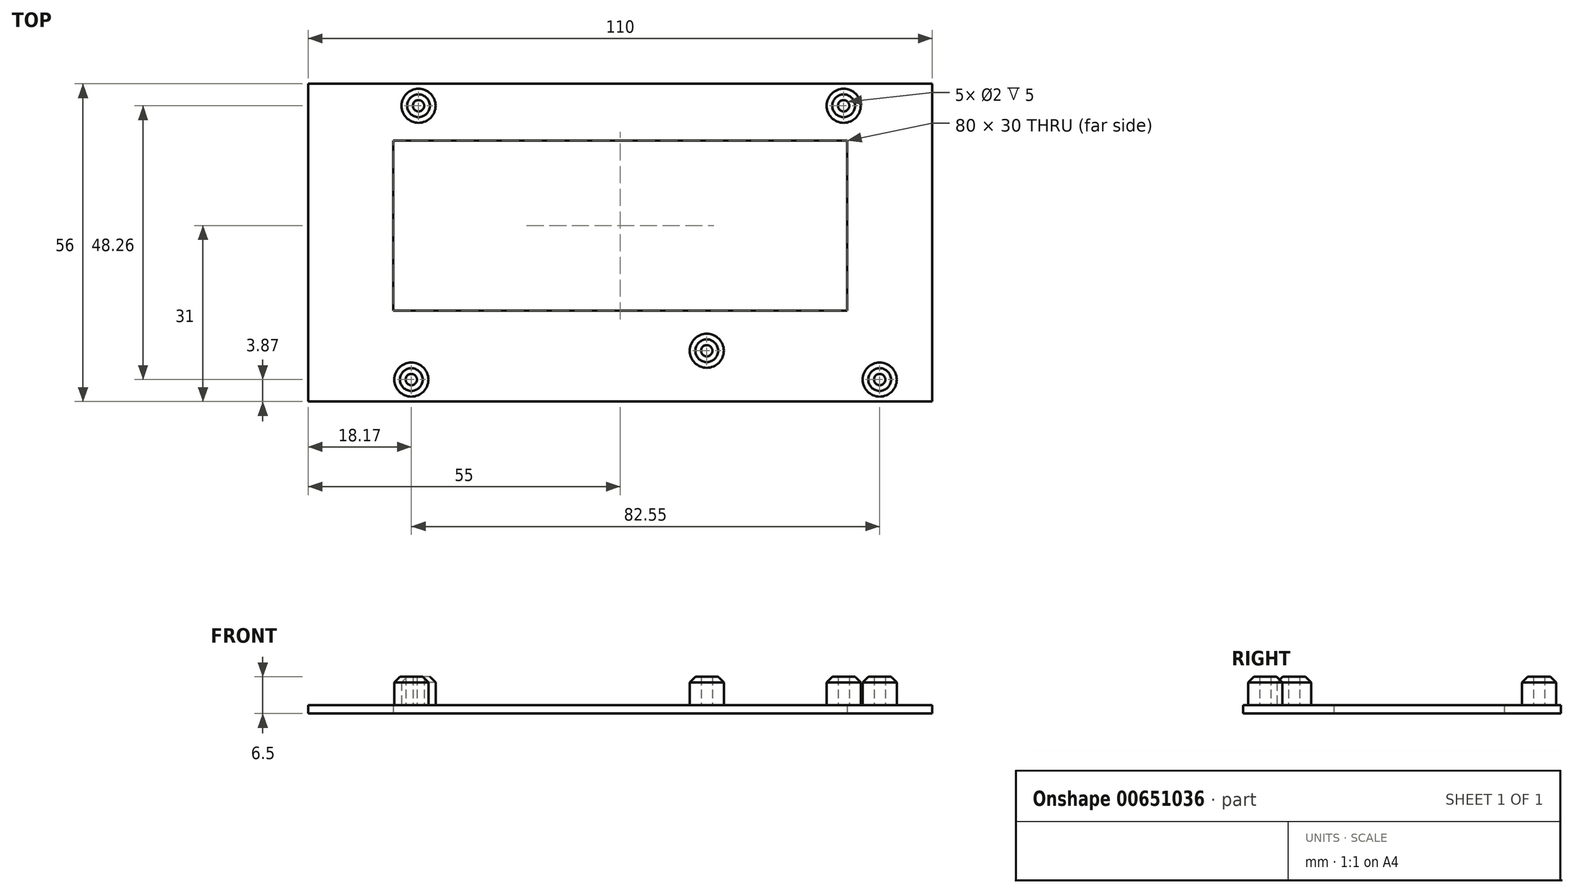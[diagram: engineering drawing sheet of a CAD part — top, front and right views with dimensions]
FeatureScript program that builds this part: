
annotation { "Feature Type Name" : "Feature", "Feature Type Description" : "" }
export const myFeature = defineFeature(function(context is Context, id is Id, definition is map)
    precondition{}
    {
        {
            var Q0;
            Q0=qCreatedBy(makeId("Top.planeOp"),FACE);
            var sketch = newSketch(context, id + "F0", { "sketchPlane" : qUnion([Q0])});
            skLineSegment(sketch, "E0.bottom", {"start": v(55, -28) * mm, "end": v(-55, -28) * mm});
            skLineSegment(sketch, "E0.top", {"start": v(55, 28) * mm, "end": v(-55, 28) * mm});
            skLineSegment(sketch, "E0.left", {"start": v(55, -28) * mm, "end": v(55, 28) * mm});
            skLineSegment(sketch, "E0.right", {"start": v(-55, -28) * mm, "end": v(-55, 28) * mm});
            skLineSegment(sketch, "E1.bottom", {"start": v(40, -12) * mm, "end": v(-40, -12) * mm});
            skLineSegment(sketch, "E1.top", {"start": v(40, 18) * mm, "end": v(-40, 18) * mm});
            skLineSegment(sketch, "E1.left", {"start": v(40, -12) * mm, "end": v(40, 18) * mm});
            skLineSegment(sketch, "E1.right", {"start": v(-40, -12) * mm, "end": v(-40, 18) * mm});
            skPoint(sketch, "E1.middle", {"position": v(0, 3) * mm});
            skSolve(sketch);
        }
        {
            var Q0;
            Q0 = qSketchRegion(id + "F0", true);
            extrude(context, id + "F1", {"entities" : qUnion([Q0]), "depth" : 1.5 * mm, "offsetDistance" : 25 * mm});
        }
        {
            var Q0;
            Q0=makeQuery(id+"F1.opExtrude","CAP_FACE",FACE,{"disambiguationData":[OSD([sQuery(id+"F0.wireOp",EDGE,"E0.bottom"),sQuery(id+"F0.wireOp",EDGE,"E0.top"),sQuery(id+"F0.wireOp",EDGE,"E0.left"),sQuery(id+"F0.wireOp",EDGE,"E0.right"),sQuery(id+"F0.wireOp",EDGE,"E1.bottom"),sQuery(id+"F0.wireOp",EDGE,"E1.top"),sQuery(id+"F0.wireOp",EDGE,"E1.left"),sQuery(id+"F0.wireOp",EDGE,"E1.right")])],"isStart":false});
            var sketch = newSketch(context, id + "F2", { "sketchPlane" : qUnion([Q0])});
            skLineSegment(sketch, "E2.left", {"start": v(50.8, -26.67) * mm, "end": v(50.8, 26.67) * mm});
            skLineSegment(sketch, "E2.right", {"start": v(-50.8, -26.67) * mm, "end": v(-50.8, 26.67) * mm});
            skPoint(sketch, "E2.middle", {"position": v(0, 0) * mm});
            skCircle(sketch, "E3", {"center": v(39.37, 24.13) * mm, "radius": 1 * mm});
            skCircle(sketch, "E4", {"center": v(-35.56, 24.13) * mm, "radius": 1 * mm});
            skCircle(sketch, "E5", {"center": v(-36.83, -24.13) * mm, "radius": 1 * mm});
            skCircle(sketch, "E6", {"center": v(15.24, -19.05) * mm, "radius": 1 * mm});
            skCircle(sketch, "E7", {"center": v(45.72, -24.13) * mm, "radius": 1 * mm});
            skCircle(sketch, "E8", {"center": v(-35.56, 24.13) * mm, "radius": 3 * mm});
            skCircle(sketch, "E9", {"center": v(39.37, 24.13) * mm, "radius": 3 * mm});
            skCircle(sketch, "E10", {"center": v(-36.83, -24.13) * mm, "radius": 3 * mm});
            skCircle(sketch, "E11", {"center": v(15.24, -19.05) * mm, "radius": 3 * mm});
            skCircle(sketch, "E12", {"center": v(45.72, -24.13) * mm, "radius": 3 * mm});
            skSolve(sketch);
        }
        {
            var Q0;
            Q0 = qSketchRegion(id + "F2", true);
            extrude(context, id + "F3", {"entities" : qUnion([Q0]), "operationType" : NewBodyOperationType.ADD, "depth" : 5 * mm, "offsetDistance" : 25 * mm});
        }
        {
            var Q0;
            Q0=makeQuery(id+"F3.opExtrude","CAP_EDGE",EDGE,{"disambiguationData":[OSD([sQuery(id+"F2.wireOp",EDGE,"E8")])],"isStart":true});
            var Q1;
            Q1=makeQuery(id+"F3.opExtrude","CAP_EDGE",EDGE,{"disambiguationData":[OSD([sQuery(id+"F2.wireOp",EDGE,"E9")])],"isStart":true});
            var Q2;
            Q2=makeQuery(id+"F3.opExtrude","CAP_EDGE",EDGE,{"disambiguationData":[OSD([sQuery(id+"F2.wireOp",EDGE,"E12")])],"isStart":true});
            var Q3;
            Q3=makeQuery(id+"F3.opExtrude","CAP_EDGE",EDGE,{"disambiguationData":[OSD([sQuery(id+"F2.wireOp",EDGE,"E11")])],"isStart":true});
            var Q4;
            Q4=makeQuery(id+"F3.opExtrude","CAP_EDGE",EDGE,{"disambiguationData":[OSD([sQuery(id+"F2.wireOp",EDGE,"E10")])],"isStart":true});
            var Q5;
            Q5=makeQuery(id+"F3.opExtrude","CAP_EDGE",EDGE,{"disambiguationData":[OSD([sQuery(id+"F2.wireOp",EDGE,"E10")])],"isStart":false});
            var Q6;
            Q6=makeQuery(id+"F3.opExtrude","CAP_EDGE",EDGE,{"disambiguationData":[OSD([sQuery(id+"F2.wireOp",EDGE,"E8")])],"isStart":false});
            var Q7;
            Q7=makeQuery(id+"F3.opExtrude","CAP_EDGE",EDGE,{"disambiguationData":[OSD([sQuery(id+"F2.wireOp",EDGE,"E9")])],"isStart":false});
            var Q8;
            Q8=makeQuery(id+"F3.opExtrude","CAP_EDGE",EDGE,{"disambiguationData":[OSD([sQuery(id+"F2.wireOp",EDGE,"E12")])],"isStart":false});
            var Q9;
            Q9=makeQuery(id+"F3.opExtrude","CAP_EDGE",EDGE,{"disambiguationData":[OSD([sQuery(id+"F2.wireOp",EDGE,"E11")])],"isStart":false});
            chamfer(context, id + "F4", {"entities" : qUnion([Q0, Q1, Q2, Q3, Q4, Q5, Q6, Q7, Q8, Q9]), "width" : 1 * mm, "tangentPropagation" : true});
        }
    });
